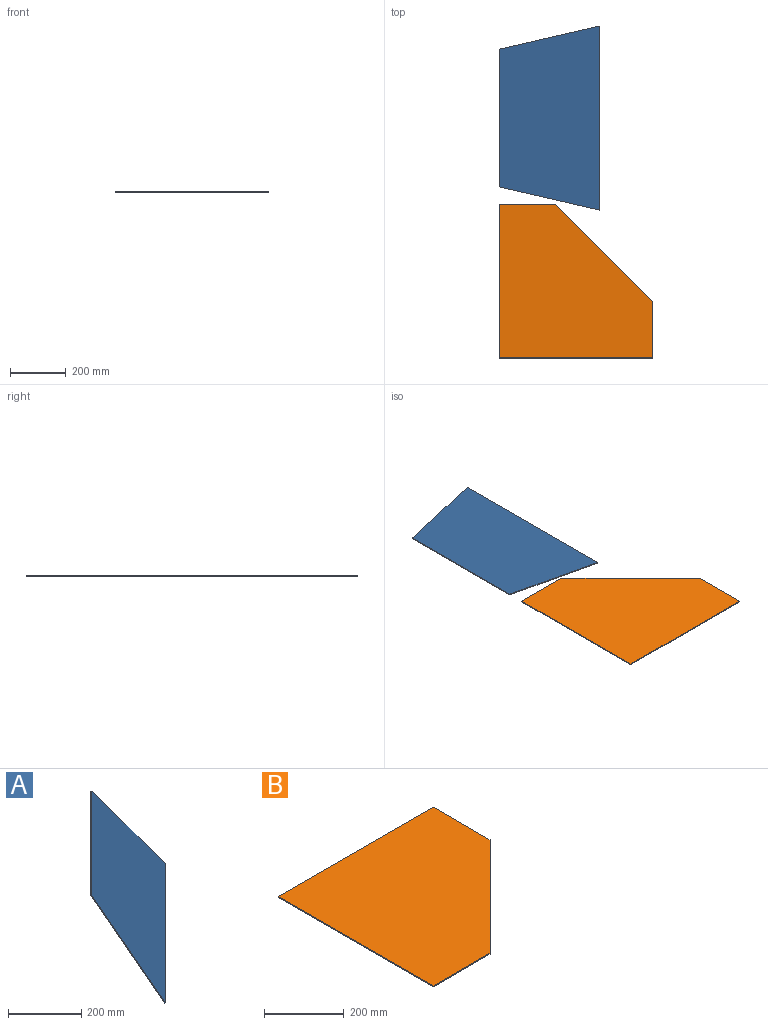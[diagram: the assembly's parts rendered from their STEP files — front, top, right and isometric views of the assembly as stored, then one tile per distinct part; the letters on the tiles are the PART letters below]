
ASSEMBLY  parts=2 mates=2
PART A: 6 faces, bbox 549.6x549.6x301.7 mm
  f0: plane 301.66x201.77mm, normal (-0.78,-0.6,0.19), area 1109.8mm2, adj f1,f3,f4,f5
  f1: plane 349.61x349.61mm, normal (-0.39,0.39,0.83), area 1475.8mm2, adj f0,f2,f4,f5
  f2: plane 301.66x201.77mm, normal (0.6,0.78,0.19), area 1109.8mm2, adj f1,f3,f4,f5
  f3: plane 466.77x466.77mm, normal (0.39,-0.39,-0.83), area 1972.8mm2, adj f0,f2,f4,f5
  f4: plane 547.84x547.84mm, normal (0.59,-0.59,0.55), area 207235mm2, adj f0,f1,f2,f3
  f5: plane 547.84x547.84mm, normal (-0.59,0.59,-0.55), area 207235mm2, adj f0,f1,f2,f3
PART B: 7 faces, bbox 550x550x3 mm
  f0: plane 550x3mm, normal (-1,0,0), area 1650mm2, adj f1,f4,f5,f6
  f1: plane 202.16x3mm, normal (0,-1,0), area 606.5mm2, adj f0,f2,f5,f6
  f2: plane 347.84x347.84mm, normal (0.71,-0.71,0), area 1475.8mm2, adj f1,f3,f5,f6
  f3: plane 202.16x3mm, normal (1,0,0), area 606.5mm2, adj f2,f4,f5,f6
  f4: plane 550x3mm, normal (0,1,0), area 1650mm2, adj f0,f3,f5,f6
  f5: plane 550x550mm, normal (0,0,1), area 242002.7mm2, adj f0,f1,f2,f3,f4
  f6: plane 550x550mm, normal (0,0,-1), area 242002.7mm2, adj f0,f1,f2,f3,f4
PLACE A rot(axis=(-0.31,-0.75,0.58),70.9deg) t=(-202.3,857.04,-847.28)mm
PLACE B rot(axis=(0,0,1),90deg) t=(-200,-200,-303)mm
MATE planar A.f4 <-> B.f5  axis (0,0,1) through (188.94,857.04,0)mm
MATE planar B.f4 <-> A.f1  axis (-1,0,0) through (0,275,-1.5)mm
